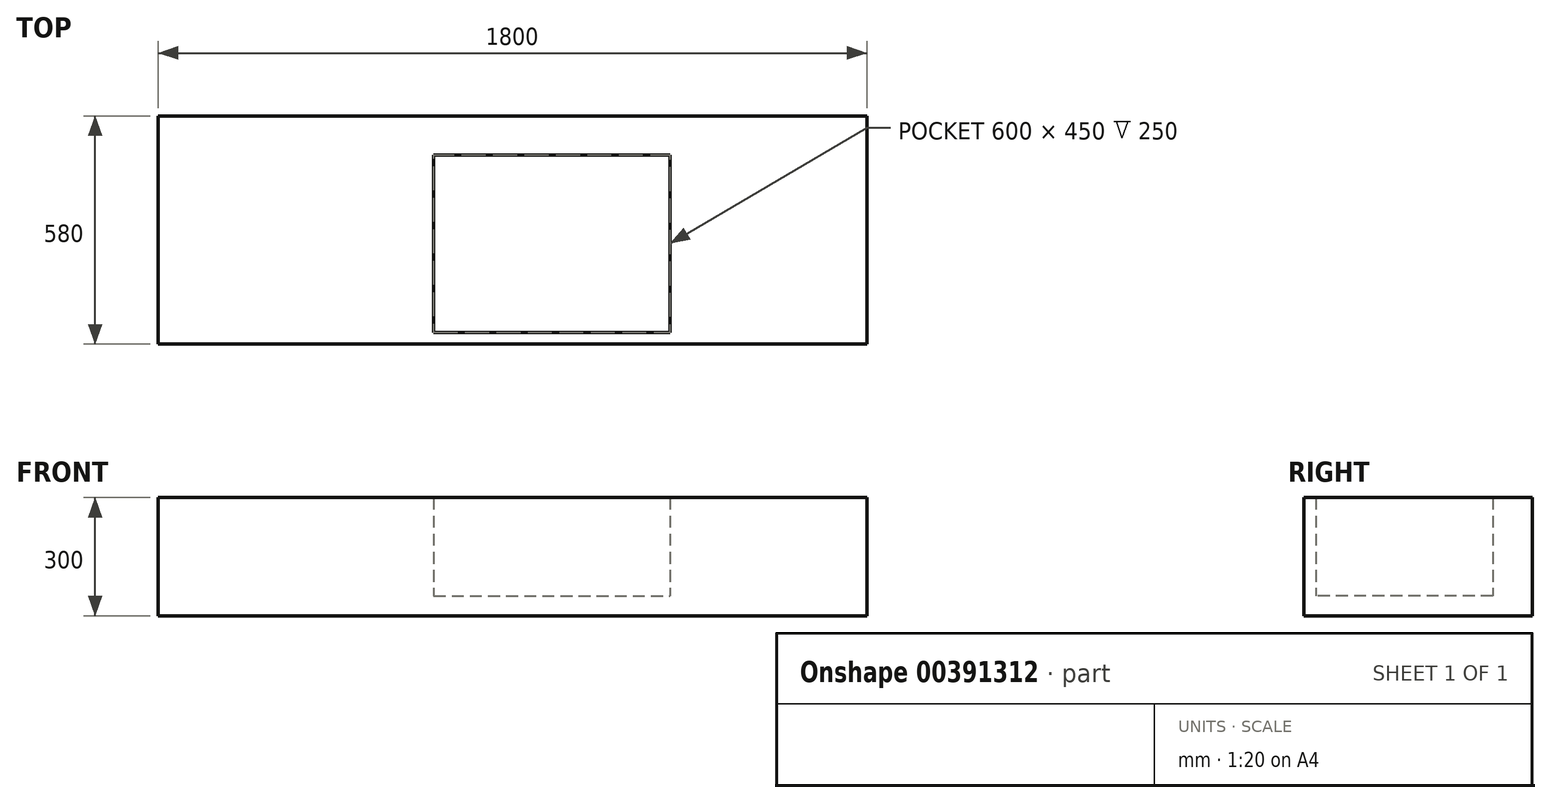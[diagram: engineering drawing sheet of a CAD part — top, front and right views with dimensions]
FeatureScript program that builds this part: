
annotation { "Feature Type Name" : "Feature", "Feature Type Description" : "" }
export const myFeature = defineFeature(function(context is Context, id is Id, definition is map)
    precondition{}
    {
        {
            var Q0;
            Q0=qCreatedBy(makeId("Top.planeOp"),FACE);
            var sketch = newSketch(context, id + "F0", { "sketchPlane" : qUnion([Q0])});
            skLineSegment(sketch, "E0.bottom", {"start": v(900, -290) * mm, "end": v(-900, -290) * mm});
            skLineSegment(sketch, "E0.top", {"start": v(900, 290) * mm, "end": v(-900, 290) * mm});
            skLineSegment(sketch, "E0.left", {"start": v(900, -290) * mm, "end": v(900, 290) * mm});
            skLineSegment(sketch, "E0.right", {"start": v(-900, -290) * mm, "end": v(-900, 290) * mm});
            skPoint(sketch, "E0.middle", {"position": v(0, 0) * mm});
            skLineSegment(sketch, "E1.bottom", {"start": v(-200, 190) * mm, "end": v(400, 190) * mm});
            skLineSegment(sketch, "E1.top", {"start": v(-200, -260) * mm, "end": v(400, -260) * mm});
            skLineSegment(sketch, "E1.left", {"start": v(-200, 190) * mm, "end": v(-200, -260) * mm});
            skLineSegment(sketch, "E1.right", {"start": v(400, 190) * mm, "end": v(400, -260) * mm});
            skSolve(sketch);
        }
        {
            var Q0;
            Q0=makeQuery(id+"F0.imprint","IMPRINT",FACE,{"disambiguationData":[TD([[makeQuery(id+"F0.imprint","IMPRINT",EDGE,{"derivedFrom":sQuery(id+"F0.wireOp",EDGE,"E0.bottom")}),-1.0]])]});
            extrude(context, id + "F1", {"entities" : qUnion([Q0]), "depth" : 250 * mm});
        }
        {
            var Q0;
            Q0=makeQuery(id+"F1.opExtrude","SWEPT_FACE",FACE,{"disambiguationData":[OSD([sQuery(id+"F0.wireOp",EDGE,"E0.left")])]});
            var sketch = newSketch(context, id + "F2", { "sketchPlane" : qUnion([Q0])});
            skLineSegment(sketch, "E2.bottom", {"start": v(-290, 0) * mm, "end": v(290, 0) * mm});
            skLineSegment(sketch, "E2.top", {"start": v(-290, -50) * mm, "end": v(290, -50) * mm});
            skLineSegment(sketch, "E2.left", {"start": v(-290, 0) * mm, "end": v(-290, -50) * mm});
            skLineSegment(sketch, "E2.right", {"start": v(290, 0) * mm, "end": v(290, -50) * mm});
            skSolve(sketch);
        }
        {
            var Q0;
            Q0=makeQuery(id+"F2.imprint","IMPRINT",FACE,{"disambiguationData":[TD([[makeQuery(id+"F2.imprint","IMPRINT",EDGE,{"derivedFrom":sQuery(id+"F2.wireOp",EDGE,"E2.bottom")}),-1.0]])]});
            extrude(context, id + "F3", {"entities" : qUnion([Q0]), "operationType" : NewBodyOperationType.ADD, "oppositeDirection" : true, "depth" : 1800 * mm});
        }
    });
